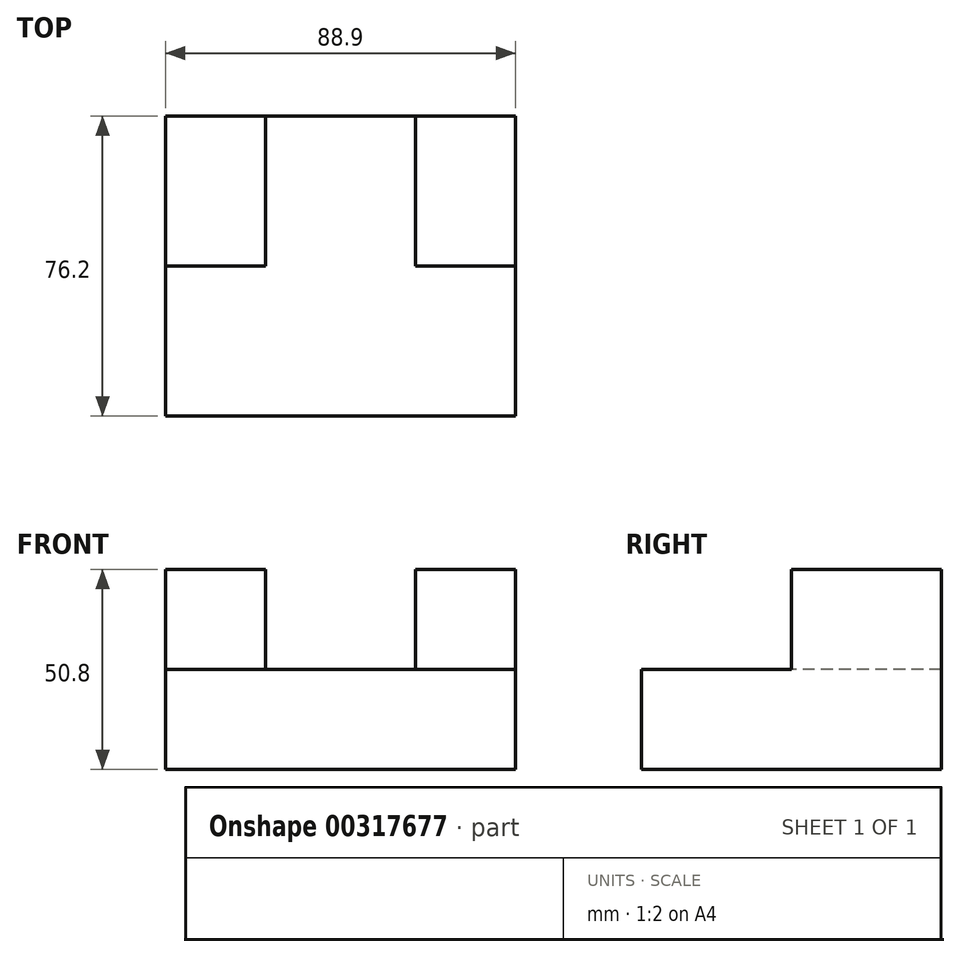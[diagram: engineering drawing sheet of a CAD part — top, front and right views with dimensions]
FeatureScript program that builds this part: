
annotation { "Feature Type Name" : "Feature", "Feature Type Description" : "" }
export const myFeature = defineFeature(function(context is Context, id is Id, definition is map)
    precondition{}
    {
        {
            var Q0;
            Q0=qCreatedBy(makeId("Front.planeOp"),FACE);
            var sketch = newSketch(context, id + "F0", { "sketchPlane" : qUnion([Q0])});
            skLineSegment(sketch, "E0", {"start": v(-51.06, -31.8) * mm, "end": v(37.84, -31.8) * mm});
            skLineSegment(sketch, "E1", {"start": v(-51.06, -31.8) * mm, "end": v(-51.06, -6.4) * mm});
            skLineSegment(sketch, "E2", {"start": v(-51.06, -6.4) * mm, "end": v(37.84, -6.4) * mm});
            skLineSegment(sketch, "E3", {"start": v(37.84, -31.8) * mm, "end": v(37.84, -6.4) * mm});
            skSolve(sketch);
        }
        {
            var Q0;
            Q0 = qSketchRegion(id + "F0", true);
            extrude(context, id + "F1", {"entities" : qUnion([Q0]), "depth" : 76.2 * mm});
        }
        {
            var Q0;
            Q0=makeQuery(id+"F1.opExtrude","SWEPT_FACE",FACE,{"disambiguationData":[OSD([sQuery(id+"F0.wireOp",EDGE,"E2")])]});
            var sketch = newSketch(context, id + "F2", { "sketchPlane" : qUnion([Q0])});
            skLineSegment(sketch, "E4", {"start": v(-51.06, 0) * mm, "end": v(-51.06, -38.1) * mm});
            skLineSegment(sketch, "E5", {"start": v(-51.06, -38.1) * mm, "end": v(-25.66, -38.1) * mm});
            skLineSegment(sketch, "E6", {"start": v(-25.66, -38.1) * mm, "end": v(-25.66, 0) * mm});
            skLineSegment(sketch, "E7", {"start": v(-25.66, 0) * mm, "end": v(-51.06, 0) * mm});
            skLineSegment(sketch, "E8", {"start": v(37.84, 0) * mm, "end": v(37.84, -38.1) * mm});
            skLineSegment(sketch, "E9", {"start": v(37.84, 0) * mm, "end": v(12.44, 0) * mm});
            skLineSegment(sketch, "E10", {"start": v(12.44, 0) * mm, "end": v(12.44, -38.1) * mm});
            skLineSegment(sketch, "E11", {"start": v(12.44, -38.1) * mm, "end": v(37.84, -38.1) * mm});
            skSolve(sketch);
        }
        {
            var Q0;
            Q0=makeQuery(id+"F2.imprint","IMPRINT",FACE,{"disambiguationData":[TD([[makeQuery(id+"F2.imprint","IMPRINT",EDGE,{"derivedFrom":sQuery(id+"F2.wireOp",EDGE,"E4")}),-1.0]])]});
            extrude(context, id + "F3", {"entities" : qUnion([Q0]), "operationType" : NewBodyOperationType.ADD, "depth" : 25.4 * mm});
        }
        {
            var Q0;
            Q0=makeQuery(id+"F2.imprint","IMPRINT",FACE,{"disambiguationData":[TD([[makeQuery(id+"F2.imprint","IMPRINT",EDGE,{"derivedFrom":sQuery(id+"F2.wireOp",EDGE,"E8")}),1.0]])]});
            extrude(context, id + "F4", {"entities" : qUnion([Q0]), "operationType" : NewBodyOperationType.ADD, "depth" : 25.4 * mm});
        }
    });
